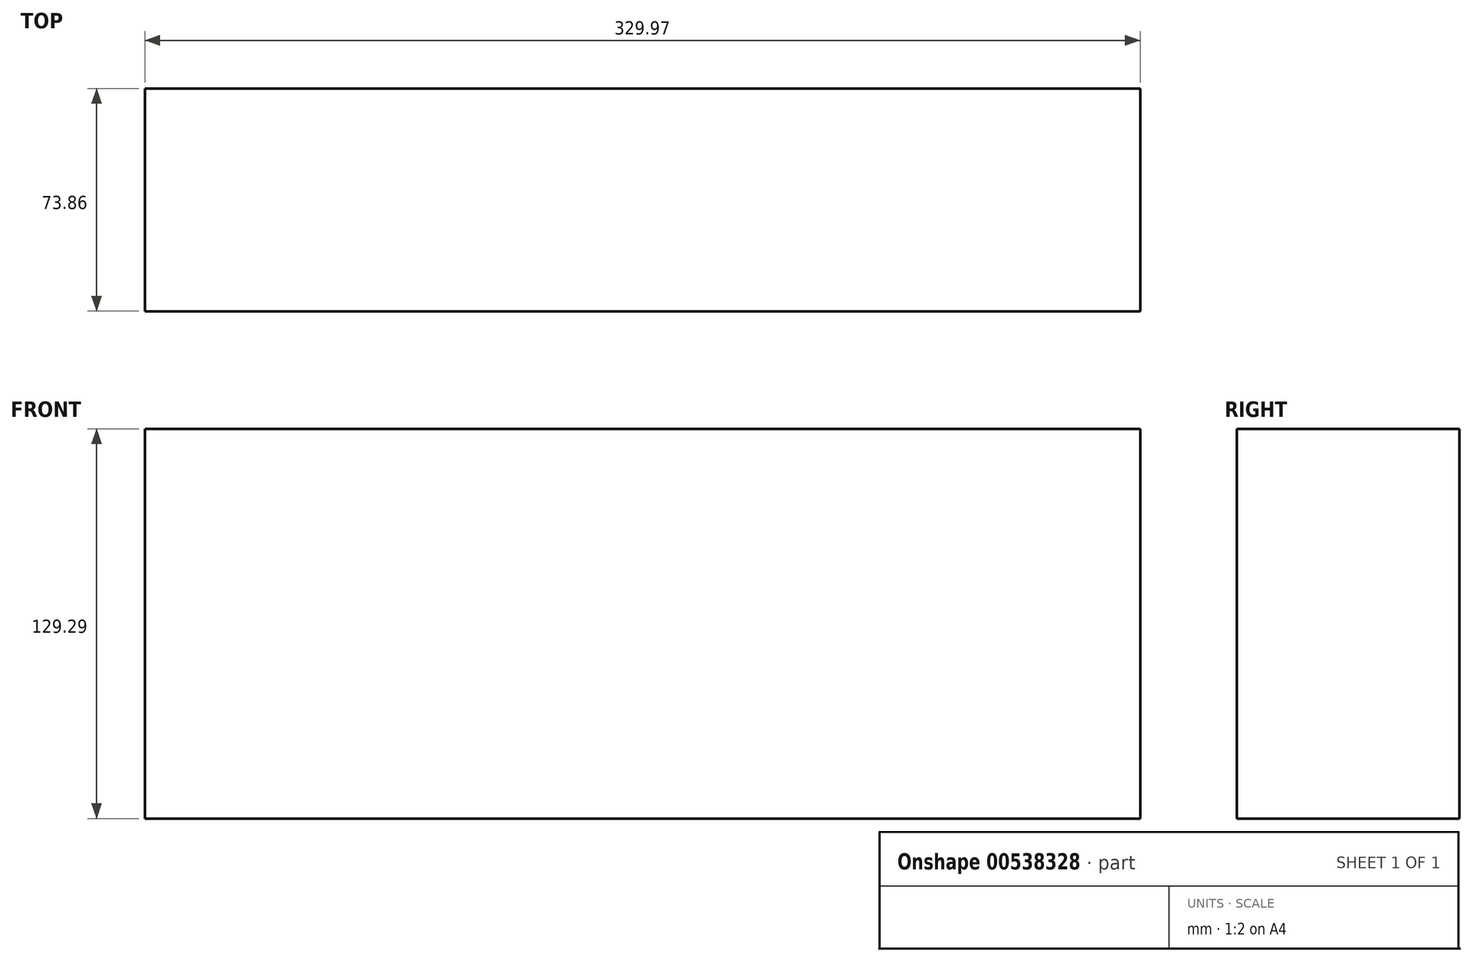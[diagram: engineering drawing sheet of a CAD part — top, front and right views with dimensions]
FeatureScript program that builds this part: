
annotation { "Feature Type Name" : "Feature", "Feature Type Description" : "" }
export const myFeature = defineFeature(function(context is Context, id is Id, definition is map)
    precondition{}
    {
        {
            var Q0;
            Q0=qCreatedBy(makeId("Top.planeOp"),FACE);
            var sketch = newSketch(context, id + "F0", { "sketchPlane" : qUnion([Q0])});
            skLineSegment(sketch, "E0.bottom", {"start": v(-200.1, -126.46) * mm, "end": v(129.86, -126.46) * mm});
            skLineSegment(sketch, "E0.top", {"start": v(-200.1, -200.32) * mm, "end": v(129.86, -200.32) * mm});
            skLineSegment(sketch, "E0.left", {"start": v(-200.1, -126.46) * mm, "end": v(-200.1, -200.32) * mm});
            skLineSegment(sketch, "E0.right", {"start": v(129.86, -126.46) * mm, "end": v(129.86, -200.32) * mm});
            skSolve(sketch);
        }
        {
            var Q0;
            Q0 = qSketchRegion(id + "F0", true);
            extrude(context, id + "F1", {"entities" : qUnion([Q0]), "depth" : 129.29 * mm, "offsetDistance" : 25.4 * mm});
        }
    });
